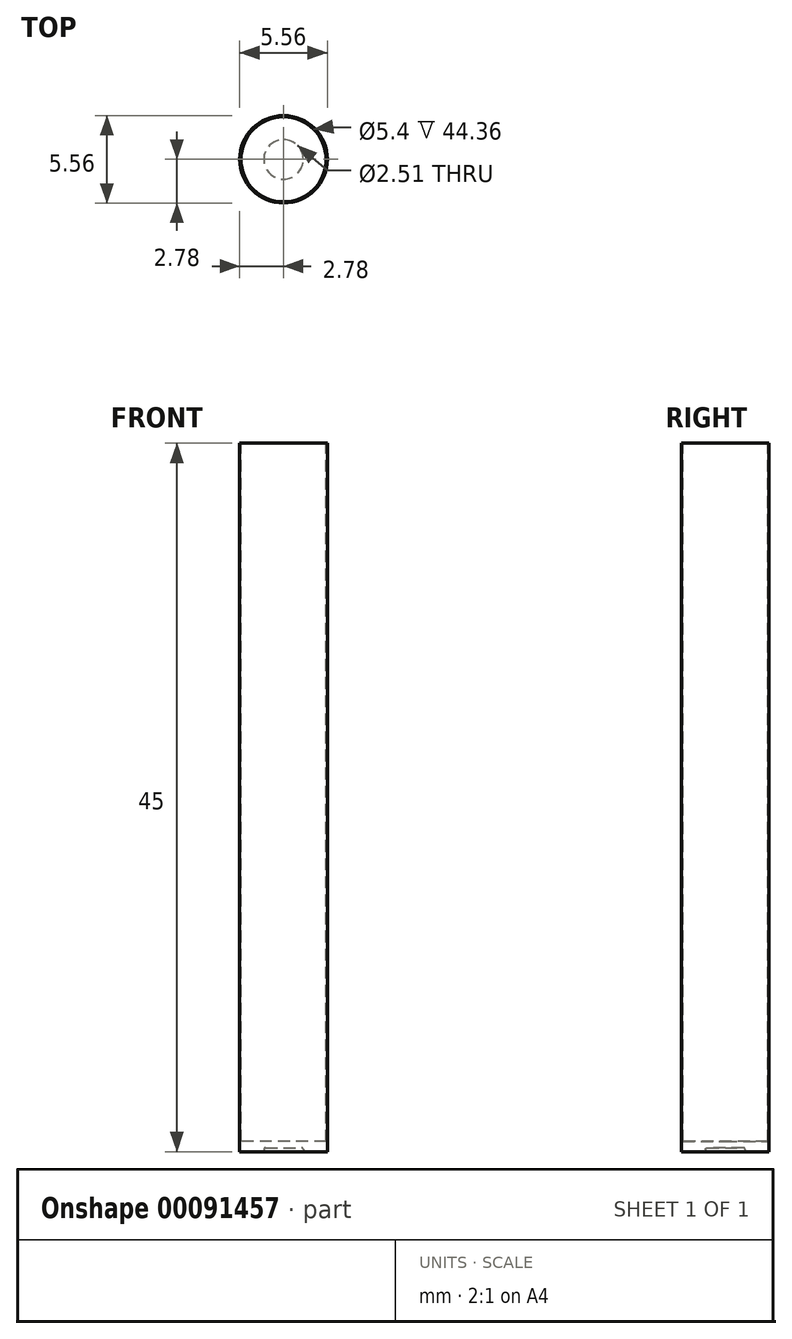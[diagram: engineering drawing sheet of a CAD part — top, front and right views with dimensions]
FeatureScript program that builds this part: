
annotation { "Feature Type Name" : "Feature", "Feature Type Description" : "" }
export const myFeature = defineFeature(function(context is Context, id is Id, definition is map)
    precondition{}
    {
        {
            var Q0;
            Q0=qCreatedBy(makeId("Top.planeOp"),FACE);
            var sketch = newSketch(context, id + "F0", { "sketchPlane" : qUnion([Q0])});
            skCircle(sketch, "E0", {"center": v(0, 0) * mm, "radius": 2.78 * mm});
            skSolve(sketch);
        }
        {
            var Q0;
            Q0=makeQuery(id+"F0.imprint","IMPRINT",FACE,{"disambiguationData":[TD([[makeQuery(id+"F0.imprint","IMPRINT",EDGE,{"derivedFrom":sQuery(id+"F0.wireOp",EDGE,"E0")}),1.0]])]});
            extrude(context, id + "F1", {"entities" : qUnion([Q0]), "depth" : 45 * mm});
        }
        {
            var Q0;
            Q0=makeQuery(id+"F1.opExtrude","CAP_FACE",FACE,{"disambiguationData":[OSD([sQuery(id+"F0.wireOp",EDGE,"E0")])],"isStart":false});
            var sketch = newSketch(context, id + "F2", { "sketchPlane" : qUnion([Q0])});
            skCircle(sketch, "E1", {"center": v(0, 0) * mm, "radius": 2.7 * mm});
            skSolve(sketch);
        }
        {
            var Q0;
            Q0 = qSketchRegion(id + "F2", true);
            extrude(context, id + "F3", {"entities" : qUnion([Q0]), "operationType" : NewBodyOperationType.REMOVE, "oppositeDirection" : true, "depth" : 44.36 * mm});
        }
        {
            var Q0;
            Q0=makeQuery(id+"F1.opExtrude","CAP_FACE",FACE,{"disambiguationData":[OSD([sQuery(id+"F0.wireOp",EDGE,"E0")])],"isStart":true});
            var sketch = newSketch(context, id + "F4", { "sketchPlane" : qUnion([Q0])});
            skCircle(sketch, "E2", {"center": v(0, 0) * mm, "radius": 1.25 * mm});
            skSolve(sketch);
        }
        {
            var Q0;
            Q0=makeQuery(id+"F4.imprint","IMPRINT",FACE,{"disambiguationData":[TD([[makeQuery(id+"F4.imprint","IMPRINT",EDGE,{"derivedFrom":sQuery(id+"F4.wireOp",EDGE,"E2")}),1.0]])]});
            extrude(context, id + "F5", {"entities" : qUnion([Q0]), "operationType" : NewBodyOperationType.REMOVE, "oppositeDirection" : true, "depth" : 0.25 * mm});
        }
        {
            var Q0;
            Q0=makeQuery(id+"F5.boolean.opBoolean","COPY",EDGE,{"derivedFrom":makeQuery(id+"F5.opExtrude","CAP_EDGE",EDGE,{"disambiguationData":[OSD([sQuery(id+"F4.wireOp",EDGE,"E2")])],"isStart":false})});
            fillet(context, id + "F6", {"entities" : qUnion([Q0]), "radius" : 0.1 * mm, "tangentPropagation" : true, "allowEdgeOverflow" : false});
        }
    });
